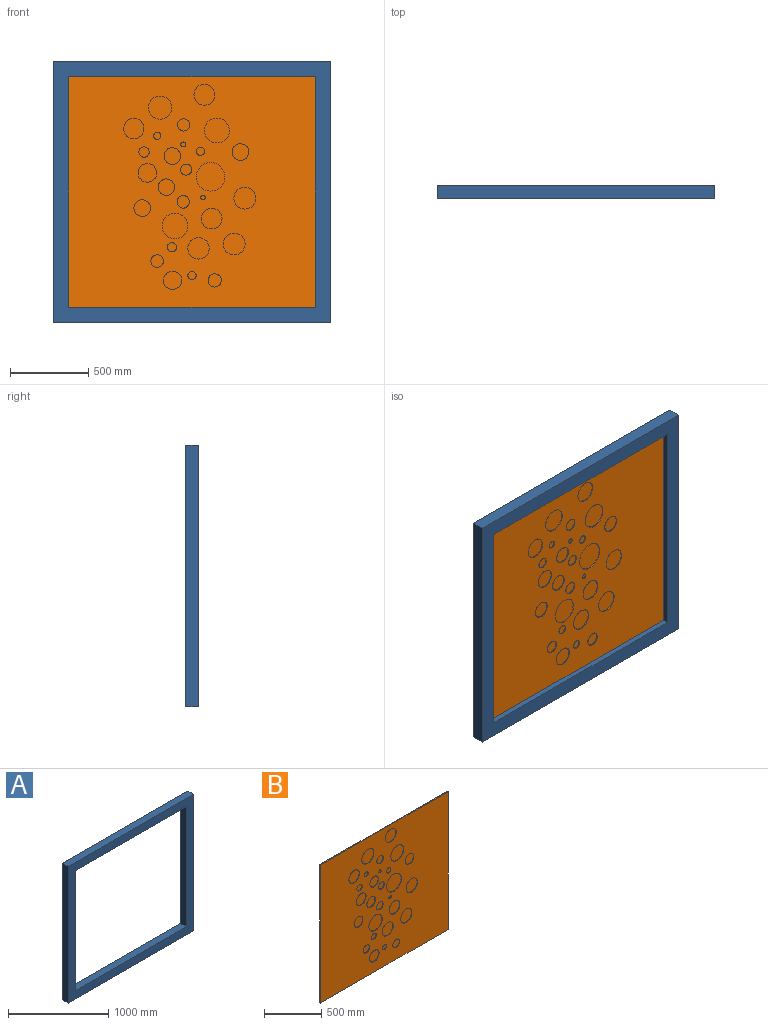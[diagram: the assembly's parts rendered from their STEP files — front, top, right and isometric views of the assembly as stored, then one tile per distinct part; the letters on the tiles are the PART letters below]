
ASSEMBLY  parts=2 mates=1
PART A: 10 faces, bbox 1770x80x1670 mm
  f0: plane 1570x80mm, normal (0,0,1), area 125600mm2, adj f1,f7,f8,f9
  f1: plane 1470x80mm, normal (1,0,0), area 117600mm2, adj f0,f2,f8,f9
  f2: plane 1570x80mm, normal (0,0,-1), area 125600mm2, adj f1,f7,f8,f9
  f3: plane 1670x80mm, normal (-1,0,0), area 133600mm2, adj f4,f6,f8,f9
  f4: plane 1770x80mm, normal (0,0,-1), area 141600mm2, adj f3,f5,f8,f9
  f5: plane 1670x80mm, normal (1,0,0), area 133600mm2, adj f4,f6,f8,f9
  f6: plane 1770x80mm, normal (0,0,1), area 141600mm2, adj f3,f5,f8,f9
  f7: plane 1470x80mm, normal (-1,0,0), area 117600mm2, adj f0,f2,f8,f9
  f8: plane 1770x1670mm, normal (0,-1,0), area 648000mm2, adj f0,f1,f2,f3,f4,f5,f6,f7
  f9: plane 1770x1670mm, normal (0,1,0), area 648000mm2, adj f0,f1,f2,f3,f4,f5,f6,f7
PART B: 62 faces, bbox 1570x10x1470 mm
  f0: plane 1570x10mm, normal (0,0,1), area 15700mm2, adj f1,f3,f4,f5
  f1: plane 1470x10mm, normal (-1,0,0), area 14700mm2, adj f0,f2,f4,f5
  f2: plane 1570x10mm, normal (0,0,-1), area 15700mm2, adj f1,f3,f4,f5
  f3: plane 1470x10mm, normal (1,0,0), area 14700mm2, adj f0,f2,f4,f5
  f4: plane 1570x1470mm, normal (0,-1,0), area 2043065.3mm2, adj f0,f1,f2,f3,f6,f8,f10,f12
  f5: plane 1570x1470mm, normal (0,1,0), area 2307900mm2, adj f0,f1,f2,f3
  f6: cylinder r=66.53mm len=133.05mm, axis (0,-1,0), area 2090mm2, adj f4,f7
  f7: plane 133.05x133.05mm, normal (0,-1,0), area 13903.8mm2, adj f6
  f8: cylinder r=59.61mm len=119.23mm, axis (0,-1,0), area 1872.8mm2, adj f4,f9
  f9: plane 119.23x119.23mm, normal (0,-1,0), area 11164.8mm2, adj f8
  f10: cylinder r=26.2mm len=52.4mm, axis (0,-1,0), area 823.1mm2, adj f4,f11
  f11: plane 52.4x52.4mm, normal (0,-1,0), area 2156.4mm2, adj f10
  f12: cylinder r=29.3mm len=58.6mm, axis (0,-1,0), area 920.4mm2, adj f4,f13
  f13: plane 58.6x58.6mm, normal (0,-1,0), area 2696.7mm2, adj f12
  f14: cylinder r=39.75mm len=79.5mm, axis (0,-1,0), area 1248.8mm2, adj f4,f15
  f15: plane 79.5x79.5mm, normal (0,-1,0), area 4964.1mm2, adj f14
  f16: cylinder r=53.01mm len=106.02mm, axis (0,-1,0), area 1665.4mm2, adj f4,f17
  f17: plane 106.02x106.02mm, normal (0,-1,0), area 8828.8mm2, adj f16
  f18: cylinder r=69.76mm len=139.51mm, axis (0,-1,0), area 2191.5mm2, adj f4,f19
  f19: plane 139.51x139.51mm, normal (0,-1,0), area 15287.2mm2, adj f18
  f20: cylinder r=26.14mm len=52.29mm, axis (0,-1,0), area 821.3mm2, adj f4,f21
  f21: plane 52.29x52.29mm, normal (0,-1,0), area 2147.1mm2, adj f20
  f22: cylinder r=53.32mm len=106.64mm, axis (0,-1,0), area 1675.1mm2, adj f4,f23
  f23: plane 106.64x106.64mm, normal (0,-1,0), area 8931.9mm2, adj f22
  f24: cylinder r=35.38mm len=70.77mm, axis (0,-1,0), area 1111.6mm2, adj f4,f25
  f25: plane 70.77x70.77mm, normal (0,-1,0), area 3933.5mm2, adj f24
  f26: cylinder r=14.79mm len=29.58mm, axis (0,-1,0), area 464.6mm2, adj f4,f27
  f27: plane 29.58x29.58mm, normal (0,-1,0), area 687.1mm2, adj f26
  f28: cylinder r=69.52mm len=139.04mm, axis (0,-1,0), area 2184.1mm2, adj f4,f29
  f29: plane 139.04x139.04mm, normal (0,-1,0), area 15184.2mm2, adj f28
  f30: cylinder r=79.26mm len=158.52mm, axis (0,-1,0), area 2490mm2, adj f4,f31
  f31: plane 158.52x158.52mm, normal (0,-1,0), area 19736mm2, adj f30
  f32: cylinder r=15.6mm len=31.19mm, axis (0,-1,0), area 490mm2, adj f4,f33
  f33: plane 31.19x31.19mm, normal (0,-1,0), area 764.2mm2, adj f32
  f34: cylinder r=38.99mm len=77.98mm, axis (0,-1,0), area 1225mm2, adj f4,f35
  f35: plane 77.98x77.98mm, normal (0,-1,0), area 4776.4mm2, adj f34
  f36: cylinder r=74.19mm len=148.37mm, axis (0,-1,0), area 2330.7mm2, adj f4,f37
  f37: plane 148.37x148.37mm, normal (0,-1,0), area 17290.5mm2, adj f36
  f38: cylinder r=52.31mm len=104.63mm, axis (0,-1,0), area 1643.5mm2, adj f4,f39
  f39: plane 104.63x104.63mm, normal (0,-1,0), area 8597.5mm2, adj f38
  f40: cylinder r=81.98mm len=163.95mm, axis (0,-1,0), area 2575.3mm2, adj f4,f41
  f41: plane 163.95x163.95mm, normal (0,-1,0), area 21111.6mm2, adj f40
  f42: cylinder r=90.94mm len=181.89mm, axis (0,-1,0), area 2857.1mm2, adj f4,f43
  f43: plane 181.89x181.89mm, normal (0,-1,0), area 25983.5mm2, adj f42
  f44: cylinder r=52.95mm len=105.9mm, axis (0,-1,0), area 1663.4mm2, adj f4,f45
  f45: plane 105.9x105.9mm, normal (0,-1,0), area 8807.7mm2, adj f44
  f46: cylinder r=42.14mm len=84.28mm, axis (0,-1,0), area 1323.9mm2, adj f4,f47
  f47: plane 84.28x84.28mm, normal (0,-1,0), area 5578.8mm2, adj f46
  f48: cylinder r=64.67mm len=129.35mm, axis (0,-1,0), area 2031.8mm2, adj f4,f49
  f49: plane 129.35x129.35mm, normal (0,-1,0), area 13140.2mm2, adj f48
  f50: cylinder r=23.15mm len=46.3mm, axis (0,-1,0), area 727.2mm2, adj f4,f51
  f51: plane 46.3x46.3mm, normal (0,-1,0), area 1683.3mm2, adj f50
  f52: cylinder r=32.82mm len=65.64mm, axis (0,-1,0), area 1031mm2, adj f4,f53
  f53: plane 65.64x65.64mm, normal (0,-1,0), area 3383.8mm2, adj f52
  f54: cylinder r=66.17mm len=132.34mm, axis (0,-1,0), area 2078.8mm2, adj f4,f55
  f55: plane 132.34x132.34mm, normal (0,-1,0), area 13756mm2, adj f54
  f56: cylinder r=40.14mm len=80.29mm, axis (0,-1,0), area 1261.2mm2, adj f4,f57
  f57: plane 80.29x80.29mm, normal (0,-1,0), area 5063mm2, adj f56
  f58: cylinder r=58.46mm len=116.92mm, axis (0,-1,0), area 1836.6mm2, adj f4,f59
  f59: plane 116.92x116.92mm, normal (0,-1,0), area 10737.3mm2, adj f58
  f60: cylinder r=68.03mm len=136.06mm, axis (0,-1,0), area 2137.2mm2, adj f4,f61
  f61: plane 136.06x136.06mm, normal (0,-1,0), area 14539.3mm2, adj f60
PLACE A t=(-2.97,0.36,3.1)mm fixed
PLACE B t=(-2.97,0.36,3.1)mm
MATE planar B.f0 <-> A.f2  axis (0,0,1) through (-2.97,0.36,738.1)mm
